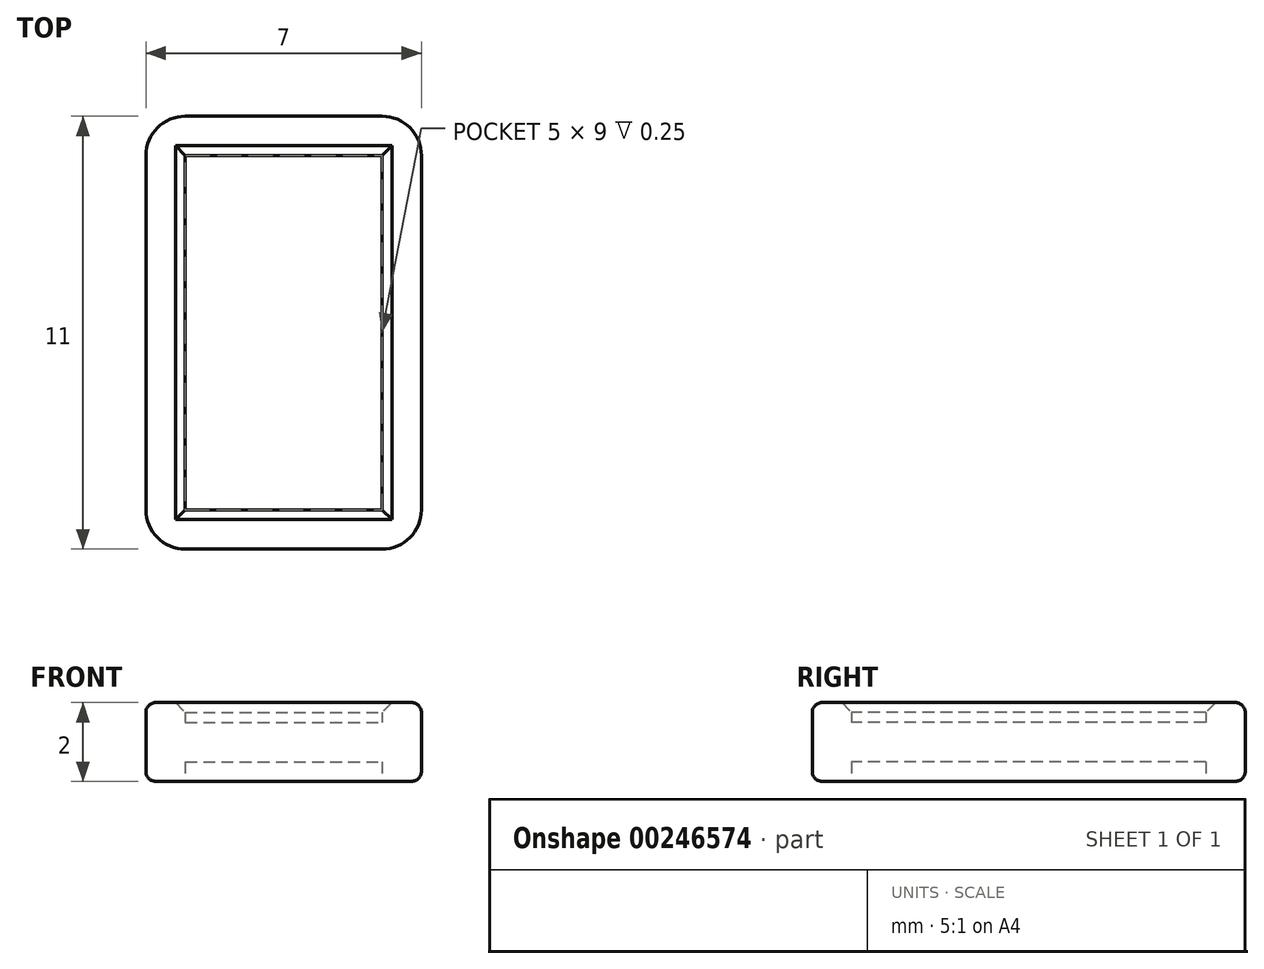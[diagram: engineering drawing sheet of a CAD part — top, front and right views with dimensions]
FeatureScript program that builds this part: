
annotation { "Feature Type Name" : "Feature", "Feature Type Description" : "" }
export const myFeature = defineFeature(function(context is Context, id is Id, definition is map)
    precondition{}
    {
        {
            var Q0;
            Q0=qCreatedBy(makeId("Top.planeOp"),FACE);
            var sketch = newSketch(context, id + "F0", { "sketchPlane" : qUnion([Q0])});
            skLineSegment(sketch, "E0.bottom", {"start": v(0, 0) * mm, "end": v(6, 0) * mm});
            skLineSegment(sketch, "E0.top", {"start": v(0, 10) * mm, "end": v(6, 10) * mm});
            skLineSegment(sketch, "E0.left", {"start": v(0, 0) * mm, "end": v(0, 10) * mm});
            skLineSegment(sketch, "E0.right", {"start": v(6, 0) * mm, "end": v(6, 10) * mm});
            skSolve(sketch);
        }
        {
            var Q0;
            Q0=makeQuery(id+"F0.imprint","IMPRINT",FACE,{"disambiguationData":[TD([[makeQuery(id+"F0.imprint","IMPRINT",EDGE,{"derivedFrom":sQuery(id+"F0.wireOp",EDGE,"E0.bottom")}),1.0]])]});
            extrude(context, id + "F1", {"entities" : qUnion([Q0]), "depth" : 1 * mm});
        }
        {
            var Q0;
            Q0=makeQuery(id+"F1.opExtrude","SWEPT_EDGE",EDGE,{"disambiguationData":[OSD([sQuery(id+"F0.wireOp",EDGE,"E0.bottom"),sQuery(id+"F0.wireOp",EDGE,"E0.left")])]});
            var Q1;
            Q1=makeQuery(id+"F1.opExtrude","SWEPT_EDGE",EDGE,{"disambiguationData":[OSD([sQuery(id+"F0.wireOp",EDGE,"E0.bottom"),sQuery(id+"F0.wireOp",EDGE,"E0.right")])]});
            var Q2;
            Q2=makeQuery(id+"F1.opExtrude","SWEPT_EDGE",EDGE,{"disambiguationData":[OSD([sQuery(id+"F0.wireOp",EDGE,"E0.top"),sQuery(id+"F0.wireOp",EDGE,"E0.right")])]});
            var Q3;
            Q3=makeQuery(id+"F1.opExtrude","SWEPT_EDGE",EDGE,{"disambiguationData":[OSD([sQuery(id+"F0.wireOp",EDGE,"E0.top"),sQuery(id+"F0.wireOp",EDGE,"E0.left")])]});
            fillet(context, id + "F2", {"entities" : qUnion([Q0, Q1, Q2, Q3]), "radius" : 0.5 * mm, "tangentPropagation" : true, "allowEdgeOverflow" : false});
        }
        {
            var Q0;
            Q0=qCreatedBy(makeId("Front.planeOp"),FACE);
            cPlane(context, id + "F3", {"entities" : qUnion([Q0]), "cplaneType" : CPlaneType.OFFSET, "offset" : 0.5 * mm, "oppositeDirection" : true, "width" : 150 * mm, "height" : 150 * mm});
        }
        {
            var Q0;
            Q0=qCreatedBy(id+"F3.planeOp",FACE);
            var sketch = newSketch(context, id + "F4", { "sketchPlane" : qUnion([Q0])});
            skLineSegment(sketch, "E1.0", {"start": v(5.5, 1) * mm, "end": v(6, 1) * mm});
            skLineSegment(sketch, "E1.1", {"start": v(6, 1) * mm, "end": v(6, 0) * mm});
            skLineSegment(sketch, "E1.2", {"start": v(6, 0) * mm, "end": v(5.5, 0) * mm});
            skLineSegment(sketch, "E2.0", {"start": v(6.5, -0.5) * mm, "end": v(5.5, -0.5) * mm});
            skLineSegment(sketch, "E2.1", {"start": v(6.5, 1.5) * mm, "end": v(6.5, -0.5) * mm});
            skLineSegment(sketch, "E2.2", {"start": v(5.5, 1.5) * mm, "end": v(6.5, 1.5) * mm});
            skLineSegment(sketch, "E3", {"start": v(5.5, 1.5) * mm, "end": v(5.5, 1) * mm});
            skLineSegment(sketch, "E4", {"start": v(5.5, 0) * mm, "end": v(5.5, -0.5) * mm});
            skSolve(sketch);
        }
        {
            var Q0;
            Q0 = qSketchRegion(id + "F4", true);
            var Q1;
            Q1=makeQuery(id+"F1.opExtrude","CAP_EDGE",EDGE,{"disambiguationData":[OSD([sQuery(id+"F0.wireOp",EDGE,"E0.right")])],"isStart":false});
            var Q2;
            {var subQ0=sQuery(id+"F0.wireOp",EDGE,"E0.right");var subQ1=sQuery(id+"F0.wireOp",EDGE,"E0.top");Q2=makeQuery(id+"F2.opFillet","BLEND_EDGE",EDGE,{"blendedFrom":[makeQuery(id+"F1.opExtrude","SWEPT_EDGE",EDGE,{"disambiguationData":[OSD([subQ1,subQ0])]}),makeQuery(id+"F1.opExtrude","CAP_FACE",FACE,{"disambiguationData":[OSD([sQuery(id+"F0.wireOp",EDGE,"E0.bottom"),subQ1,sQuery(id+"F0.wireOp",EDGE,"E0.left"),subQ0])],"isStart":false})],"blendedInto":[makeQuery(id+"F1.opExtrude","CAP_FACE",FACE,{"disambiguationData":[OSD([sQuery(id+"F0.wireOp",EDGE,"E0.bottom"),subQ1,sQuery(id+"F0.wireOp",EDGE,"E0.left"),subQ0])],"isStart":false})]});}
            var Q3;
            Q3=makeQuery(id+"F1.opExtrude","CAP_EDGE",EDGE,{"disambiguationData":[OSD([sQuery(id+"F0.wireOp",EDGE,"E0.top")])],"isStart":false});
            var Q4;
            {var subQ0=sQuery(id+"F0.wireOp",EDGE,"E0.left");var subQ1=sQuery(id+"F0.wireOp",EDGE,"E0.top");Q4=makeQuery(id+"F2.opFillet","BLEND_EDGE",EDGE,{"blendedFrom":[makeQuery(id+"F1.opExtrude","SWEPT_EDGE",EDGE,{"disambiguationData":[OSD([subQ1,subQ0])]}),makeQuery(id+"F1.opExtrude","CAP_FACE",FACE,{"disambiguationData":[OSD([sQuery(id+"F0.wireOp",EDGE,"E0.bottom"),subQ1,subQ0,sQuery(id+"F0.wireOp",EDGE,"E0.right")])],"isStart":false})],"blendedInto":[makeQuery(id+"F1.opExtrude","CAP_FACE",FACE,{"disambiguationData":[OSD([sQuery(id+"F0.wireOp",EDGE,"E0.bottom"),subQ1,subQ0,sQuery(id+"F0.wireOp",EDGE,"E0.right")])],"isStart":false})]});}
            var Q5;
            Q5=makeQuery(id+"F1.opExtrude","CAP_EDGE",EDGE,{"disambiguationData":[OSD([sQuery(id+"F0.wireOp",EDGE,"E0.left")])],"isStart":false});
            var Q6;
            {var subQ0=sQuery(id+"F0.wireOp",EDGE,"E0.left");var subQ1=sQuery(id+"F0.wireOp",EDGE,"E0.bottom");Q6=makeQuery(id+"F2.opFillet","BLEND_EDGE",EDGE,{"blendedFrom":[makeQuery(id+"F1.opExtrude","SWEPT_EDGE",EDGE,{"disambiguationData":[OSD([subQ1,subQ0])]}),makeQuery(id+"F1.opExtrude","CAP_FACE",FACE,{"disambiguationData":[OSD([subQ1,sQuery(id+"F0.wireOp",EDGE,"E0.top"),subQ0,sQuery(id+"F0.wireOp",EDGE,"E0.right")])],"isStart":false})],"blendedInto":[makeQuery(id+"F1.opExtrude","CAP_FACE",FACE,{"disambiguationData":[OSD([subQ1,sQuery(id+"F0.wireOp",EDGE,"E0.top"),subQ0,sQuery(id+"F0.wireOp",EDGE,"E0.right")])],"isStart":false})]});}
            var Q7;
            Q7=makeQuery(id+"F1.opExtrude","CAP_EDGE",EDGE,{"disambiguationData":[OSD([sQuery(id+"F0.wireOp",EDGE,"E0.bottom")])],"isStart":false});
            var Q8;
            {var subQ0=sQuery(id+"F0.wireOp",EDGE,"E0.right");var subQ1=sQuery(id+"F0.wireOp",EDGE,"E0.bottom");Q8=makeQuery(id+"F2.opFillet","BLEND_EDGE",EDGE,{"blendedFrom":[makeQuery(id+"F1.opExtrude","SWEPT_EDGE",EDGE,{"disambiguationData":[OSD([subQ1,subQ0])]}),makeQuery(id+"F1.opExtrude","CAP_FACE",FACE,{"disambiguationData":[OSD([subQ1,sQuery(id+"F0.wireOp",EDGE,"E0.top"),sQuery(id+"F0.wireOp",EDGE,"E0.left"),subQ0])],"isStart":false})],"blendedInto":[makeQuery(id+"F1.opExtrude","CAP_FACE",FACE,{"disambiguationData":[OSD([subQ1,sQuery(id+"F0.wireOp",EDGE,"E0.top"),sQuery(id+"F0.wireOp",EDGE,"E0.left"),subQ0])],"isStart":false})]});}
            sweep(context, id + "F5", {"operationType" : NewBodyOperationType.ADD, "profiles" : qUnion([Q0]), "path" : qUnion([Q1, Q2, Q3, Q4, Q5, Q6, Q7, Q8])});
        }
        {
            var Q0;
            Q0=makeQuery(id+"F5.opSweep","SWEPT_EDGE",EDGE,{"disambiguationData":[OSD([sQuery(id+"F0.wireOp",EDGE,"E0.left"),sQuery(id+"F4.wireOp",EDGE,"E2.1"),sQuery(id+"F4.wireOp",EDGE,"E2.2")])]});
            var Q1;
            Q1=makeQuery(id+"F5.opSweep","SWEPT_EDGE",EDGE,{"disambiguationData":[OSD([sQuery(id+"F0.wireOp",EDGE,"E0.left"),sQuery(id+"F4.wireOp",EDGE,"E2.0"),sQuery(id+"F4.wireOp",EDGE,"E2.1")])]});
            fillet(context, id + "F6", {"entities" : qUnion([Q0, Q1]), "radius" : .25 * mm, "tangentPropagation" : true, "allowEdgeOverflow" : false});
        }
        {
            var Q0;
            Q0=makeQuery(id+"F5.opSweep","SWEPT_EDGE",EDGE,{"disambiguationData":[OSD([sQuery(id+"F0.wireOp",EDGE,"E0.top"),sQuery(id+"F4.wireOp",EDGE,"E2.2"),sQuery(id+"F4.wireOp",EDGE,"E3")])]});
            var Q1;
            Q1=makeQuery(id+"F5.opSweep","SWEPT_EDGE",EDGE,{"disambiguationData":[OSD([sQuery(id+"F0.wireOp",EDGE,"E0.left"),sQuery(id+"F4.wireOp",EDGE,"E2.2"),sQuery(id+"F4.wireOp",EDGE,"E3")])]});
            var Q2;
            Q2=makeQuery(id+"F5.opSweep","SWEPT_EDGE",EDGE,{"disambiguationData":[OSD([sQuery(id+"F0.wireOp",EDGE,"E0.right"),sQuery(id+"F4.wireOp",EDGE,"E2.2"),sQuery(id+"F4.wireOp",EDGE,"E3")])]});
            var Q3;
            Q3=makeQuery(id+"F5.opSweep","SWEPT_EDGE",EDGE,{"disambiguationData":[OSD([sQuery(id+"F0.wireOp",EDGE,"E0.bottom"),sQuery(id+"F4.wireOp",EDGE,"E2.2"),sQuery(id+"F4.wireOp",EDGE,"E3")])]});
            chamfer(context, id + "F7", {"entities" : qUnion([Q0, Q1, Q2, Q3]), "width" : 0.25 * mm, "tangentPropagation" : true});
        }
    });
